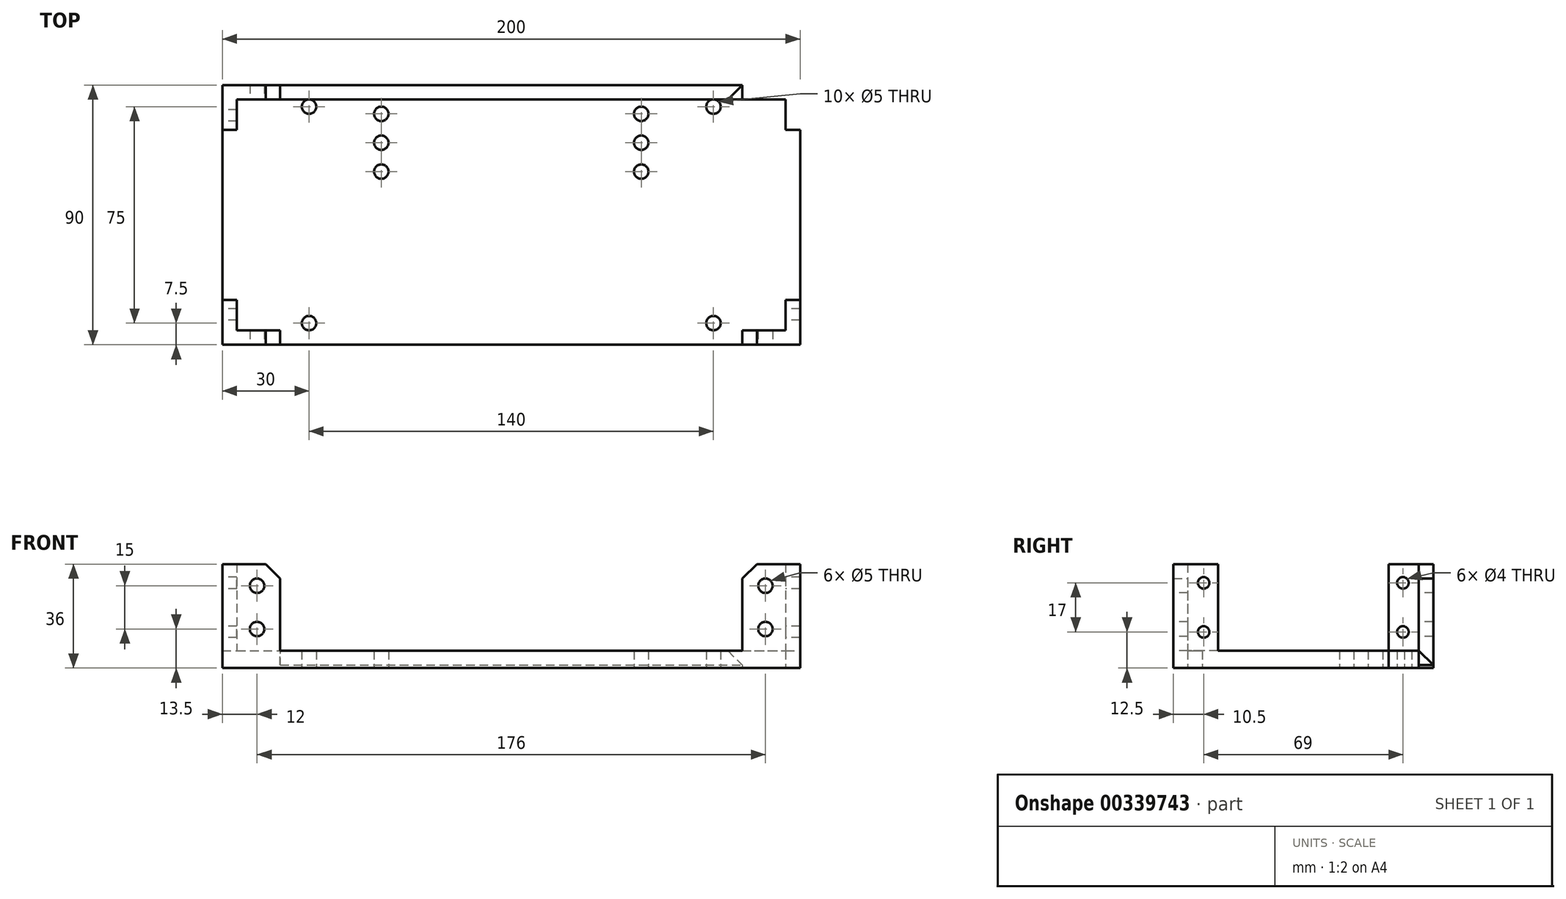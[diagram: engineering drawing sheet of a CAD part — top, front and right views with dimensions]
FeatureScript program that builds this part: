
annotation { "Feature Type Name" : "Feature", "Feature Type Description" : "" }
export const myFeature = defineFeature(function(context is Context, id is Id, definition is map)
    precondition{}
    {
        {
            var Q0;
            Q0=qCreatedBy(makeId("Top.planeOp"),FACE);
            var sketch = newSketch(context, id + "F0", { "sketchPlane" : qUnion([Q0])});
            skLineSegment(sketch, "E0.bottom", {"start": v(0, 0) * mm, "end": v(200, 0) * mm});
            skLineSegment(sketch, "E0.top", {"start": v(0, 90) * mm, "end": v(200, 90) * mm});
            skLineSegment(sketch, "E0.left", {"start": v(0, 0) * mm, "end": v(0, 90) * mm});
            skLineSegment(sketch, "E0.right", {"start": v(200, 0) * mm, "end": v(200, 90) * mm});
            skLineSegment(sketch, "E1", {"start": v(200, 90) * mm, "end": v(180, 90) * mm});
            skLineSegment(sketch, "E2", {"start": v(180, 90) * mm, "end": v(180, 85) * mm});
            skLineSegment(sketch, "E3", {"start": v(180, 85) * mm, "end": v(195, 85) * mm});
            skLineSegment(sketch, "E4", {"start": v(195, 85) * mm, "end": v(195, 74.5) * mm});
            skLineSegment(sketch, "E5", {"start": v(195, 74.5) * mm, "end": v(200, 74.5) * mm});
            skLineSegment(sketch, "E6", {"start": v(180, 0) * mm, "end": v(180, 5) * mm});
            skLineSegment(sketch, "E7", {"start": v(180, 5) * mm, "end": v(195, 5) * mm});
            skLineSegment(sketch, "E8", {"start": v(195, 5) * mm, "end": v(195, 15.5) * mm});
            skLineSegment(sketch, "E9", {"start": v(195, 15.5) * mm, "end": v(200, 15.5) * mm});
            skLineSegment(sketch, "E10", {"start": v(0, 15.5) * mm, "end": v(5, 15.5) * mm});
            skLineSegment(sketch, "E11", {"start": v(5, 15.5) * mm, "end": v(5, 5) * mm});
            skLineSegment(sketch, "E12", {"start": v(5, 5) * mm, "end": v(20, 5) * mm});
            skLineSegment(sketch, "E13", {"start": v(20, 5) * mm, "end": v(20, 0) * mm});
            skLineSegment(sketch, "E14", {"start": v(0, 74.5) * mm, "end": v(5, 74.5) * mm});
            skLineSegment(sketch, "E15", {"start": v(5, 74.5) * mm, "end": v(5, 85) * mm});
            skLineSegment(sketch, "E16", {"start": v(5, 85) * mm, "end": v(20, 85) * mm});
            skLineSegment(sketch, "E17", {"start": v(20, 85) * mm, "end": v(20, 90) * mm});
            skLineSegment(sketch, "E18", {"start": v(200, 90) * mm, "end": v(200, 74.5) * mm});
            skLineSegment(sketch, "E19", {"start": v(20, 90) * mm, "end": v(30, 90) * mm});
            skLineSegment(sketch, "E20", {"start": v(30, 90) * mm, "end": v(30, 82.5) * mm});
            skLineSegment(sketch, "E21", {"start": v(20, 0) * mm, "end": v(30, 0) * mm});
            skLineSegment(sketch, "E22", {"start": v(30, 0) * mm, "end": v(30, 7.5) * mm});
            skLineSegment(sketch, "E23", {"start": v(180, 0) * mm, "end": v(170, 0) * mm});
            skLineSegment(sketch, "E24", {"start": v(170, 0) * mm, "end": v(170, 7.5) * mm});
            skLineSegment(sketch, "E25", {"start": v(180, 90) * mm, "end": v(170, 90) * mm});
            skLineSegment(sketch, "E26", {"start": v(170, 90) * mm, "end": v(170, 82.5) * mm});
            skCircle(sketch, "E27", {"center": v(30, 82.5) * mm, "radius": 2.5 * mm});
            skCircle(sketch, "E28", {"center": v(30, 7.5) * mm, "radius": 2.5 * mm});
            skCircle(sketch, "E29", {"center": v(170, 82.5) * mm, "radius": 2.5 * mm});
            skCircle(sketch, "E30", {"center": v(170, 7.5) * mm, "radius": 2.5 * mm});
            skLineSegment(sketch, "E31", {"start": v(100, 90) * mm, "end": v(100, 60) * mm});
            skLineSegment(sketch, "E32", {"start": v(100, 60) * mm, "end": v(145, 60) * mm});
            skLineSegment(sketch, "E33", {"start": v(100, 60) * mm, "end": v(55, 60) * mm});
            skCircle(sketch, "E34", {"center": v(55, 60) * mm, "radius": 2.5 * mm});
            skCircle(sketch, "E35", {"center": v(145, 60) * mm, "radius": 2.5 * mm});
            skLineSegment(sketch, "E36", {"start": v(55, 60) * mm, "end": v(55, 70) * mm});
            skLineSegment(sketch, "E37", {"start": v(55, 70) * mm, "end": v(55, 80) * mm});
            skLineSegment(sketch, "E38", {"start": v(55, 80) * mm, "end": v(55, 90) * mm});
            skLineSegment(sketch, "E39", {"start": v(145, 60) * mm, "end": v(145, 70) * mm});
            skLineSegment(sketch, "E40", {"start": v(145, 70) * mm, "end": v(145, 80) * mm});
            skLineSegment(sketch, "E41", {"start": v(145, 80) * mm, "end": v(145, 90) * mm});
            skCircle(sketch, "E42", {"center": v(55, 80) * mm, "radius": 2.5 * mm});
            skCircle(sketch, "E43", {"center": v(55, 70) * mm, "radius": 2.5 * mm});
            skCircle(sketch, "E44", {"center": v(145, 80) * mm, "radius": 2.5 * mm});
            skCircle(sketch, "E45", {"center": v(145, 70) * mm, "radius": 2.5 * mm});
            skSolve(sketch);
        }
        {
            var Q0;
            Q0=makeQuery(id+"F0.imprint","IMPRINT",FACE,{"disambiguationData":[TD([[makeQuery(id+"F0.imprint","IMPRINT",EDGE,{"derivedFrom":sQuery(id+"F0.wireOp",EDGE,"E2")}),-1.0]])]});
            var Q1;
            Q1=makeQuery(id+"F0.imprint","IMPRINT",FACE,{"disambiguationData":[TD([[makeQuery(id+"F0.imprint","IMPRINT",EDGE,{"derivedFrom":sQuery(id+"F0.wireOp",EDGE,"E34")}),-1.0]])]});
            var Q2;
            Q2=makeQuery(id+"F0.imprint","IMPRINT",FACE,{"disambiguationData":[TD([[makeQuery(id+"F0.imprint","IMPRINT",EDGE,{"derivedFrom":sQuery(id+"F0.wireOp",EDGE,"E35")}),-1.0]])]});
            var Q3;
            Q3=makeQuery(id+"F0.imprint","IMPRINT",FACE,{"disambiguationData":[TD([[makeQuery(id+"F0.imprint","IMPRINT",EDGE,{"derivedFrom":sQuery(id+"F0.wireOp",EDGE,"E27")}),-1.0]])]});
            var Q4;
            Q4=makeQuery(id+"F0.imprint","IMPRINT",FACE,{"disambiguationData":[TD([[makeQuery(id+"F0.imprint","IMPRINT",EDGE,{"derivedFrom":sQuery(id+"F0.wireOp",EDGE,"E29")}),-1.0]])]});
            var Q5;
            Q5=makeQuery(id+"F0.imprint","IMPRINT",FACE,{"disambiguationData":[TD([[makeQuery(id+"F0.imprint","IMPRINT",EDGE,{"derivedFrom":sQuery(id+"F0.wireOp",EDGE,"E30")}),-1.0]])]});
            var Q6;
            Q6=makeQuery(id+"F0.imprint","IMPRINT",FACE,{"disambiguationData":[TD([[makeQuery(id+"F0.imprint","IMPRINT",EDGE,{"derivedFrom":sQuery(id+"F0.wireOp",EDGE,"E28")}),-1.0]])]});
            extrude(context, id + "F1", {"entities" : qUnion([Q0, Q1, Q2, Q3, Q4, Q5, Q6]), "depth" : 6 * mm});
        }
        {
            var Q0;
            Q0=makeQuery(id+"F0.imprint","IMPRINT",FACE,{"disambiguationData":[TD([[makeQuery(id+"F0.imprint","IMPRINT",EDGE,{"derivedFrom":sQuery(id+"F0.wireOp",EDGE,"E1")}),1.0]])]});
            var Q1;
            {var subQ0=sQuery(id+"F0.wireOp",EDGE,"E6");Q1=makeQuery(id+"F0.imprint","IMPRINT",FACE,{"disambiguationData":[TD([[makeQuery(id+"F0.imprint","IMPRINT",EDGE,{"derivedFrom":subQ0}),-1.0]])]});}
            var Q2;
            {var subQ3=sQuery(id+"F0.wireOp",EDGE,"E10");Q2=makeQuery(id+"F0.imprint","IMPRINT",FACE,{"disambiguationData":[TD([[makeQuery(id+"F0.imprint","IMPRINT",EDGE,{"derivedFrom":subQ3}),-1.0]])]});}
            var Q3;
            {var subQ4=sQuery(id+"F0.wireOp",EDGE,"E14");Q3=makeQuery(id+"F0.imprint","IMPRINT",FACE,{"disambiguationData":[TD([[makeQuery(id+"F0.imprint","IMPRINT",EDGE,{"derivedFrom":subQ4}),1.0]])]});}
            extrude(context, id + "F2", {"entities" : qUnion([Q0, Q1, Q2, Q3]), "operationType" : NewBodyOperationType.ADD, "depth" : 36 * mm});
        }
        {
            var Q0;
            Q0=makeQuery(id+"F1.opExtrude","CAP_EDGE",EDGE,{"disambiguationData":[OSD([sQuery(id+"F0.wireOp",EDGE,"E2")])],"isStart":false});
            var Q1;
            Q1=makeQuery(id+"F1.opExtrude","CAP_EDGE",EDGE,{"disambiguationData":[OSD([sQuery(id+"F0.wireOp",EDGE,"E6")])],"isStart":false});
            var Q2;
            Q2=makeQuery(id+"F2.opExtrude","CAP_EDGE",EDGE,{"disambiguationData":[OSD([sQuery(id+"F0.wireOp",EDGE,"E6")])],"isStart":false});
            var Q3;
            Q3=makeQuery(id+"F2.opExtrude","CAP_EDGE",EDGE,{"disambiguationData":[OSD([sQuery(id+"F0.wireOp",EDGE,"E2")])],"isStart":false});
            var Q4;
            Q4=makeQuery(id+"F2.opExtrude","CAP_EDGE",EDGE,{"disambiguationData":[OSD([sQuery(id+"F0.wireOp",EDGE,"E17")])],"isStart":false});
            var Q5;
            Q5=makeQuery(id+"F2.opExtrude","CAP_EDGE",EDGE,{"disambiguationData":[OSD([sQuery(id+"F0.wireOp",EDGE,"E13")])],"isStart":false});
            var Q6;
            Q6=makeQuery(id+"F1.opExtrude","CAP_EDGE",EDGE,{"disambiguationData":[OSD([sQuery(id+"F0.wireOp",EDGE,"E17")])],"isStart":false});
            var Q7;
            Q7=makeQuery(id+"F1.opExtrude","CAP_EDGE",EDGE,{"disambiguationData":[OSD([sQuery(id+"F0.wireOp",EDGE,"E13")])],"isStart":false});
            chamfer(context, id + "F3", {"entities" : qUnion([Q0, Q1, Q2, Q3, Q4, Q5, Q6, Q7]), "width" : 5 * mm, "tangentPropagation" : true});
        }
        {
            var Q0;
            {var subQ0=sQuery(id+"F0.wireOp",EDGE,"E0.bottom");var subQ1=sQuery(id+"F0.wireOp",EDGE,"E23");var subQ2=sQuery(id+"F0.wireOp",EDGE,"E21");Q0=makeQuery(id+"F2.boolean.opBoolean","MERGE",FACE,{"derivedFrom":[makeQuery(id+"F1.opExtrude","SWEPT_FACE",FACE,{"disambiguationData":[OSD([subQ0,subQ2,subQ1])]}),makeQuery(id+"F2.opExtrude","SWEPT_FACE",FACE,{"disambiguationData":[OSD([subQ0]),TDD([makeQuery(id+"F0.imprint","IMPRINT",EDGE,{"disambiguationData":[TD([[makeQuery(id+"F0.imprint","INTERSECT",VERTEX,{"derivedFrom":[subQ0,sQuery(id+"F0.wireOp",EDGE,"E0.left")]}),-1.0]])],"derivedFrom":subQ0})])]}),makeQuery(id+"F2.opExtrude","SWEPT_FACE",FACE,{"disambiguationData":[OSD([subQ0]),TDD([makeQuery(id+"F0.imprint","IMPRINT",EDGE,{"disambiguationData":[TD([[makeQuery(id+"F0.imprint","INTERSECT",VERTEX,{"derivedFrom":[subQ0,sQuery(id+"F0.wireOp",EDGE,"E0.right")]}),1.0]])],"derivedFrom":subQ0})])]})]});}
            var sketch = newSketch(context, id + "F4", { "sketchPlane" : qUnion([Q0])});
            skLineSegment(sketch, "E46", {"start": v(20, 21) * mm, "end": v(0, 21) * mm});
            skLineSegment(sketch, "E47", {"start": v(180, 21) * mm, "end": v(200, 21) * mm});
            skLineSegment(sketch, "E48", {"start": v(200, 21) * mm, "end": v(188, 21) * mm});
            skLineSegment(sketch, "E49", {"start": v(188, 21) * mm, "end": v(188, 13.5) * mm});
            skLineSegment(sketch, "E50", {"start": v(188, 21) * mm, "end": v(188, 28.5) * mm});
            skLineSegment(sketch, "E51", {"start": v(12, 21) * mm, "end": v(12, 28.5) * mm});
            skLineSegment(sketch, "E52", {"start": v(12, 21) * mm, "end": v(12, 13.5) * mm});
            skCircle(sketch, "E53", {"center": v(12, 28.5) * mm, "radius": 2.5 * mm});
            skCircle(sketch, "E54", {"center": v(12, 13.5) * mm, "radius": 2.5 * mm});
            skCircle(sketch, "E55", {"center": v(188, 28.5) * mm, "radius": 2.5 * mm});
            skCircle(sketch, "E56", {"center": v(188, 13.5) * mm, "radius": 2.5 * mm});
            skLineSegment(sketch, "E57", {"start": v(100, 6) * mm, "end": v(117.93, 6) * mm});
            skLineSegment(sketch, "E58", {"start": v(100, 6) * mm, "end": v(82.07, 6) * mm});
            skSolve(sketch);
        }
        {
            var Q0;
            {var subQ0=sQuery(id+"F0.wireOp",EDGE,"E0.left");Q0=makeQuery(id+"F2.boolean.opBoolean","MERGE",FACE,{"derivedFrom":[makeQuery(id+"F1.opExtrude","SWEPT_FACE",FACE,{"disambiguationData":[OSD([subQ0])]}),makeQuery(id+"F2.opExtrude","SWEPT_FACE",FACE,{"disambiguationData":[OSD([subQ0]),TDD([makeQuery(id+"F0.imprint","IMPRINT",EDGE,{"disambiguationData":[TD([[makeQuery(id+"F0.imprint","INTERSECT",VERTEX,{"derivedFrom":[sQuery(id+"F0.wireOp",EDGE,"E0.bottom"),subQ0]}),-1.0]])],"derivedFrom":subQ0})])]}),makeQuery(id+"F2.opExtrude","SWEPT_FACE",FACE,{"disambiguationData":[OSD([subQ0]),TDD([makeQuery(id+"F0.imprint","IMPRINT",EDGE,{"disambiguationData":[TD([[makeQuery(id+"F0.imprint","INTERSECT",VERTEX,{"derivedFrom":[sQuery(id+"F0.wireOp",EDGE,"E0.top"),subQ0]}),1.0]])],"derivedFrom":subQ0})])]})]});}
            var sketch = newSketch(context, id + "F5", { "sketchPlane" : qUnion([Q0])});
            skLineSegment(sketch, "E59", {"start": v(-74.5, 21) * mm, "end": v(-79.5, 21) * mm});
            skLineSegment(sketch, "E60", {"start": v(-79.5, 21) * mm, "end": v(-79.5, 29.5) * mm});
            skLineSegment(sketch, "E61", {"start": v(-79.5, 21) * mm, "end": v(-79.5, 12.5) * mm});
            skLineSegment(sketch, "E62", {"start": v(-15.5, 21) * mm, "end": v(-10.5, 21) * mm});
            skLineSegment(sketch, "E63", {"start": v(-10.5, 21) * mm, "end": v(-10.5, 29.5) * mm});
            skLineSegment(sketch, "E64", {"start": v(-10.5, 21) * mm, "end": v(-10.5, 12.5) * mm});
            skCircle(sketch, "E65", {"center": v(-79.5, 29.5) * mm, "radius": 2 * mm});
            skCircle(sketch, "E66", {"center": v(-79.5, 12.5) * mm, "radius": 2 * mm});
            skCircle(sketch, "E67", {"center": v(-10.5, 29.5) * mm, "radius": 2 * mm});
            skCircle(sketch, "E68", {"center": v(-10.5, 12.5) * mm, "radius": 2 * mm});
            skSolve(sketch);
        }
        {
            var Q0;
            Q0=makeQuery(id+"F5.imprint","IMPRINT",FACE,{"disambiguationData":[TD([[makeQuery(id+"F5.imprint","IMPRINT",EDGE,{"derivedFrom":sQuery(id+"F5.wireOp",EDGE,"E65")}),1.0]])]});
            var Q1;
            Q1=makeQuery(id+"F5.imprint","IMPRINT",FACE,{"disambiguationData":[TD([[makeQuery(id+"F5.imprint","IMPRINT",EDGE,{"derivedFrom":sQuery(id+"F5.wireOp",EDGE,"E66")}),1.0]])]});
            var Q2;
            Q2=makeQuery(id+"F5.imprint","IMPRINT",FACE,{"disambiguationData":[TD([[makeQuery(id+"F5.imprint","IMPRINT",EDGE,{"derivedFrom":sQuery(id+"F5.wireOp",EDGE,"E67")}),1.0]])]});
            var Q3;
            Q3=makeQuery(id+"F5.imprint","IMPRINT",FACE,{"disambiguationData":[TD([[makeQuery(id+"F5.imprint","IMPRINT",EDGE,{"derivedFrom":sQuery(id+"F5.wireOp",EDGE,"E68")}),1.0]])]});
            extrude(context, id + "F6", {"entities" : qUnion([Q0, Q1, Q2, Q3]), "operationType" : NewBodyOperationType.REMOVE, "oppositeDirection" : true, "depth" : 210 * mm});
        }
        {
            var Q0;
            Q0=makeQuery(id+"F4.imprint","IMPRINT",FACE,{"disambiguationData":[TD([[makeQuery(id+"F4.imprint","IMPRINT",EDGE,{"derivedFrom":sQuery(id+"F4.wireOp",EDGE,"E53")}),1.0]])]});
            var Q1;
            Q1=makeQuery(id+"F4.imprint","IMPRINT",FACE,{"disambiguationData":[TD([[makeQuery(id+"F4.imprint","IMPRINT",EDGE,{"derivedFrom":sQuery(id+"F4.wireOp",EDGE,"E54")}),1.0]])]});
            var Q2;
            Q2=makeQuery(id+"F4.imprint","IMPRINT",FACE,{"disambiguationData":[TD([[makeQuery(id+"F4.imprint","IMPRINT",EDGE,{"derivedFrom":sQuery(id+"F4.wireOp",EDGE,"E55")}),1.0]])]});
            var Q3;
            Q3=makeQuery(id+"F4.imprint","IMPRINT",FACE,{"disambiguationData":[TD([[makeQuery(id+"F4.imprint","IMPRINT",EDGE,{"derivedFrom":sQuery(id+"F4.wireOp",EDGE,"E56")}),1.0]])]});
            extrude(context, id + "F7", {"entities" : qUnion([Q0, Q1, Q2, Q3]), "operationType" : NewBodyOperationType.REMOVE, "oppositeDirection" : true, "depth" : 100 * mm});
        }
        {
            var Q0;
            Q0=makeQuery(id+"F1.opExtrude","CAP_EDGE",EDGE,{"disambiguationData":[OSD([sQuery(id+"F0.wireOp",EDGE,"E0.top"),sQuery(id+"F0.wireOp",EDGE,"E19"),sQuery(id+"F0.wireOp",EDGE,"E25")])],"isStart":false});
            chamfer(context, id + "F8", {"entities" : qUnion([Q0]), "width" : 5 * mm, "tangentPropagation" : true});
        }
    });
